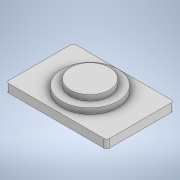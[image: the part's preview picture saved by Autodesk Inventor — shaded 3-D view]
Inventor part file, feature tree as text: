
AUTODESK INVENTOR PART (.ipt)
format: ipt  version: 2022 (Build 260153000, 153)  size: 131,584 bytes
history: native  units: in
note: dims shown in document units (in); Inventor stores cm internally (conversion verified against a paired STEP export)
features: fillet x4, extrude x3, sketch x3
ambient origin geometry x8: Origin, YZ Plane, XZ Plane, XY Plane, X Axis, Y Axis, Z Axis, Center Point
bodies: Solid1 (feature_tree)
feature tree (10):
  extrude  "Extrusion1"  Depth=4.7244in
  fillet  "Face Fillet1"
  fillet  "Face Fillet2"
  fillet  "Face Fillet3"
  fillet  "Face Fillet4"
  extrude  "Extrusion2"  Depth=0.1969in
  extrude  "Extrusion3"  Depth=0.1969in
  sketch  "Sketch1"  dims[d0=7.0866in d1=4.7244in]
  sketch  "Sketch2"  dims[d2=0.5906in d3=0.0in d4=0.1969in]
  sketch  "Sketch3"  dims[d5=0.1969in d6=0.1969in d7=0.1969in d8=3.937in d9=0.3937in d10=0.0in d11=2.7559in d12=0.3937in d13=0.0in d14=0.0197in d15=0.0344in d16=0.0197in d17=0.0344in]
